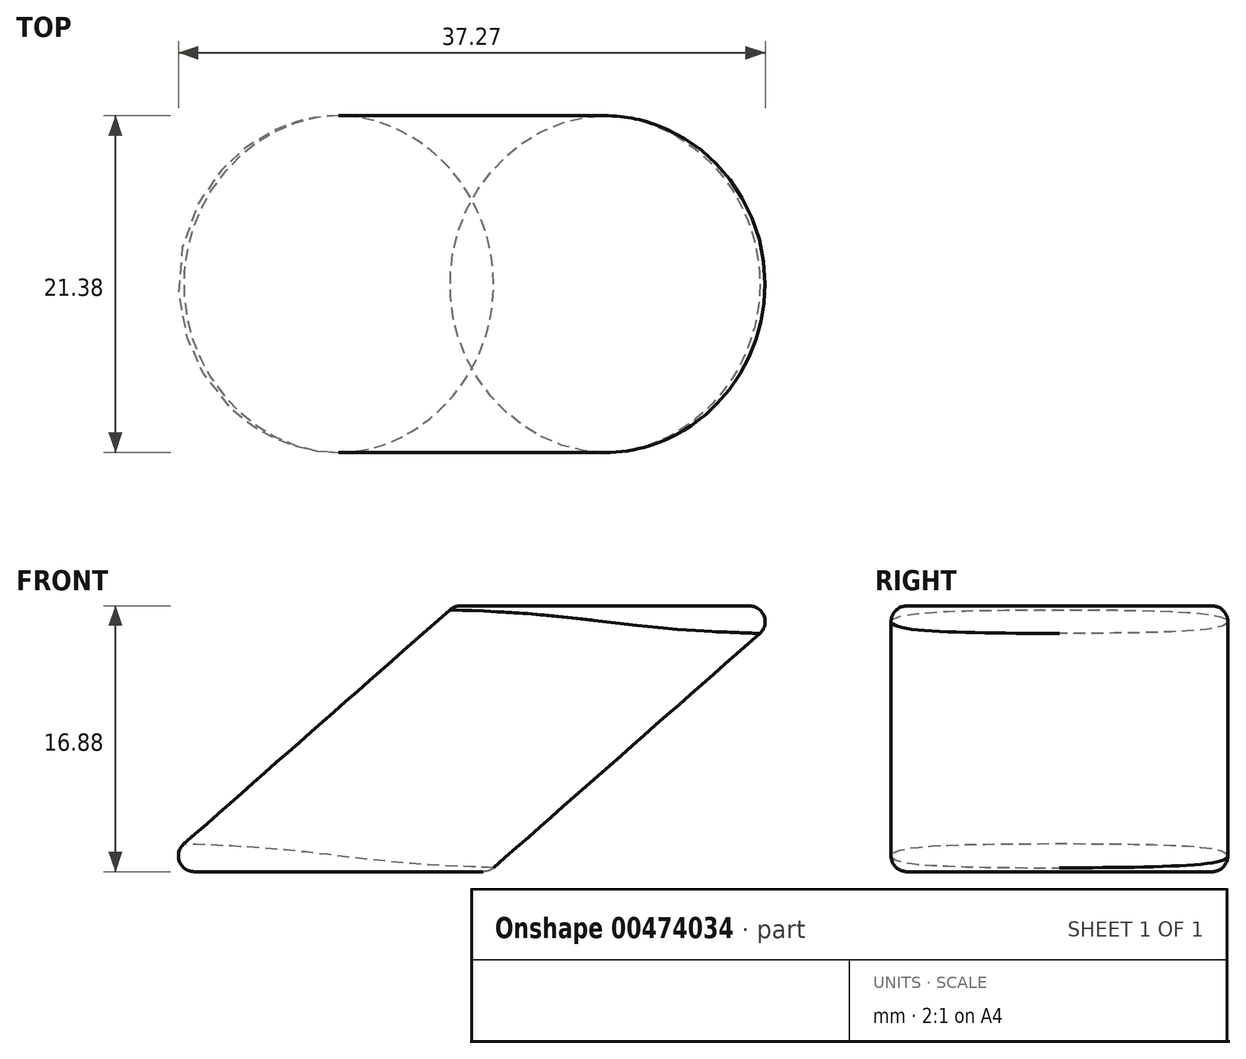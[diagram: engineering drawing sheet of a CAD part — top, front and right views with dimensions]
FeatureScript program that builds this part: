
annotation { "Feature Type Name" : "Feature", "Feature Type Description" : "" }
export const myFeature = defineFeature(function(context is Context, id is Id, definition is map)
    precondition{}
    {
        {
            var Q0;
            Q0=qCreatedBy(makeId("Front.planeOp"),FACE);
            var sketch = newSketch(context, id + "F0", { "sketchPlane" : qUnion([Q0])});
            skLineSegment(sketch, "E0", {"start": v(-9.69, 28.3) * mm, "end": v(9.5, 45.18) * mm});
            skLineSegment(sketch, "E1", {"start": v(0, 0) * mm, "end": v(0, 36.82) * mm});
            skSolve(sketch);
        }
        {
            var Q0;
            Q0=qCreatedBy(makeId("Top.planeOp"),FACE);
            var sketch = newSketch(context, id + "F1", { "sketchPlane" : qUnion([Q0])});
            skCircle(sketch, "E2", {"center": v(0, 0) * mm, "radius": 10.7 * mm});
            skSolve(sketch);
        }
        {
            var Q0;
            Q0=makeQuery(id+"F1.imprint","IMPRINT",FACE,{"disambiguationData":[TD([[makeQuery(id+"F1.imprint","IMPRINT",EDGE,{"derivedFrom":sQuery(id+"F1.wireOp",EDGE,"E2")}),1.0]])]});
            var Q1;
            Q1=sQuery(id+"F0.wireOp",EDGE,"E0");
            sweep(context, id + "F2", {"profiles" : qUnion([Q0]), "path" : qUnion([Q1])});
        }
        {
            var Q0;
            Q0=makeQuery(id+"F2.opSweep","CAP_FACE",FACE,{"disambiguationData":[OSD([sQuery(id+"F0.wireOp",VERTEX,"E0.start"),sQuery(id+"F1.wireOp",EDGE,"E2")])],"isStart":true});
            fillet(context, id + "F3", {"entities" : qUnion([Q0]), "radius" : 1 * mm, "tangentPropagation" : true, "allowEdgeOverflow" : false});
        }
        {
            var Q0;
            Q0=makeQuery(id+"F2.opSweep","CAP_EDGE",EDGE,{"disambiguationData":[OSD([sQuery(id+"F0.wireOp",VERTEX,"E0.end"),sQuery(id+"F1.wireOp",EDGE,"E2")])],"isStart":false});
            fillet(context, id + "F4", {"entities" : qUnion([Q0]), "radius" : 1 * mm, "tangentPropagation" : true, "allowEdgeOverflow" : false});
        }
    });
